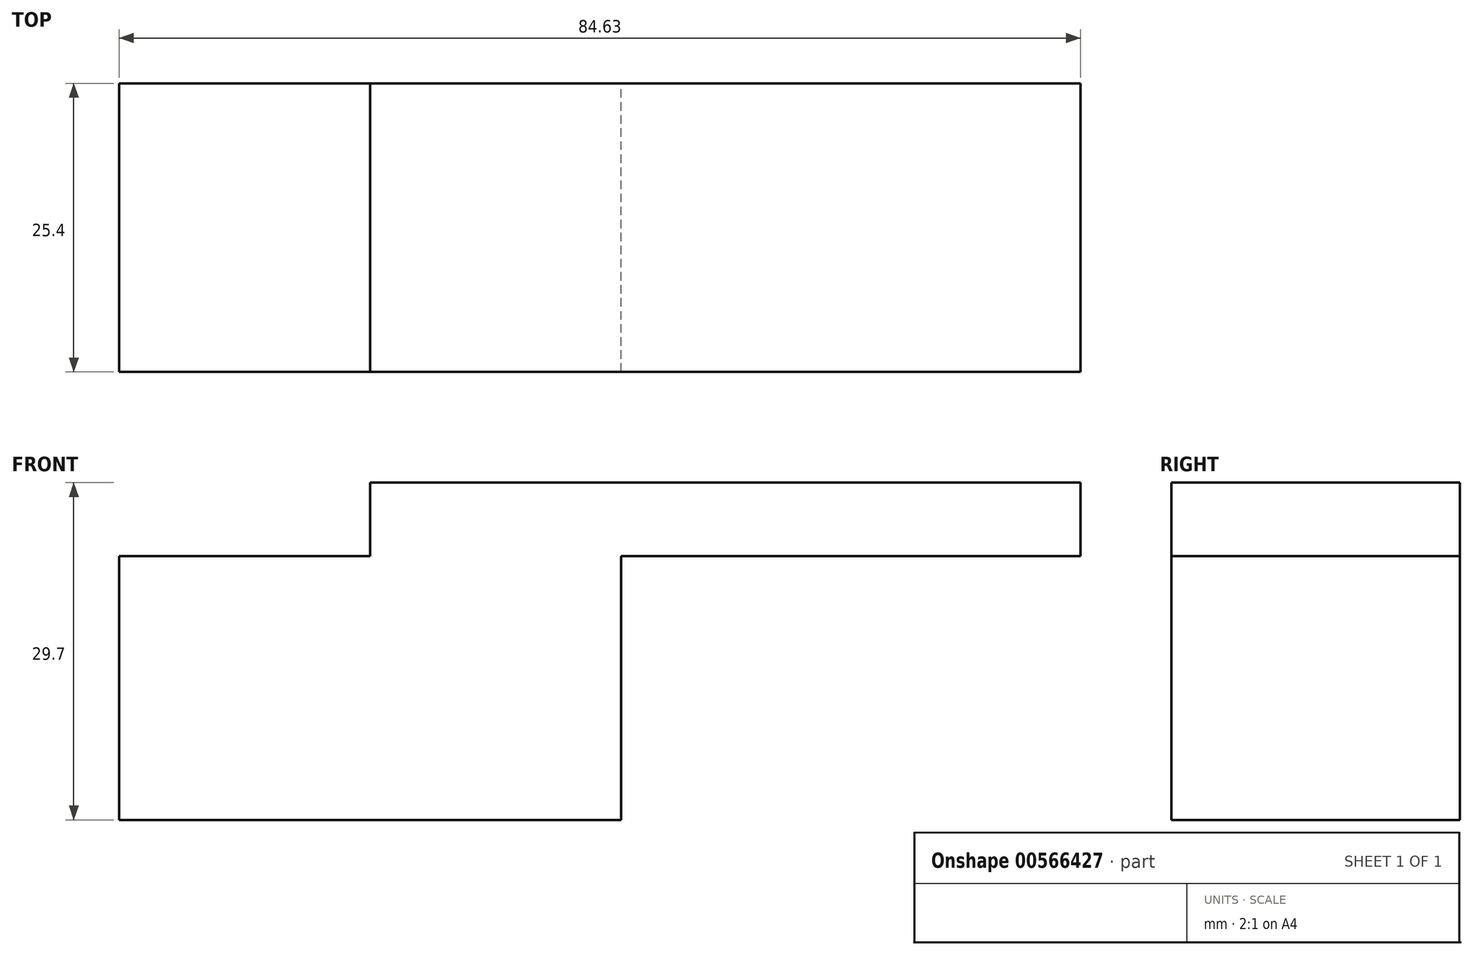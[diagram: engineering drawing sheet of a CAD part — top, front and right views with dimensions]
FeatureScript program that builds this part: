
annotation { "Feature Type Name" : "Feature", "Feature Type Description" : "" }
export const myFeature = defineFeature(function(context is Context, id is Id, definition is map)
    precondition{}
    {
        {
            var Q0;
            Q0=qCreatedBy(makeId("Front.planeOp"),FACE);
            var sketch = newSketch(context, id + "F0", { "sketchPlane" : qUnion([Q0])});
            skLineSegment(sketch, "E0.bottom", {"start": v(-67.65, 43.06) * mm, "end": v(-23.47, 43.06) * mm});
            skLineSegment(sketch, "E0.top", {"start": v(-67.65, 19.85) * mm, "end": v(-23.47, 19.85) * mm});
            skLineSegment(sketch, "E0.left", {"start": v(-67.65, 43.06) * mm, "end": v(-67.65, 19.85) * mm});
            skLineSegment(sketch, "E0.right", {"start": v(-23.47, 43.06) * mm, "end": v(-23.47, 19.85) * mm});
            skPoint(sketch, "E1.firstSnap0", {"position": v(-45.56, 43.06) * mm});
            skPoint(sketch, "E1.oppositeSnap0", {"position": v(-45.56, 43.06) * mm});
            skLineSegment(sketch, "E1.bottom", {"start": v(-45.56, 49.55) * mm, "end": v(16.98, 49.55) * mm});
            skLineSegment(sketch, "E1.top", {"start": v(-45.56, 43.06) * mm, "end": v(16.98, 43.06) * mm});
            skLineSegment(sketch, "E1.left", {"start": v(-45.56, 49.55) * mm, "end": v(-45.56, 43.06) * mm});
            skLineSegment(sketch, "E1.right", {"start": v(16.98, 49.55) * mm, "end": v(16.98, 43.06) * mm});
            skSolve(sketch);
        }
        {
            var Q0;
            Q0 = qSketchRegion(id + "F0", true);
            extrude(context, id + "F1", {"entities" : qUnion([Q0]), "depth" : 25.4 * mm, "offsetDistance" : 25.4 * mm});
        }
    });
